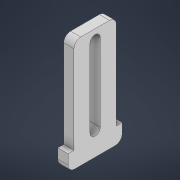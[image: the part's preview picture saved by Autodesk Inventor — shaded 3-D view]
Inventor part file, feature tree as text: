
AUTODESK INVENTOR PART (.ipt)
format: ipt  version: 2021 (Build 250183000, 183)  size: 122,368 bytes
history: native  units: mm
features: extrude x1, sketch x1
ambient origin geometry x8: Origin, YZ Plane, XZ Plane, XY Plane, X Axis, Y Axis, Z Axis, Center Point
bodies: Body1 (feature_tree)
feature tree (2):
  extrude  "Extrusion3"  Depth=2.0mm
  sketch  "Sketch1"  dims[d1=16.0mm d2=6.0mm d3=1.75mm d5=2.0mm d14=1.75mm d18=3.0mm d19=3.0mm d21=2.0mm d22=3.0mm d23=0.0mm d24=28.0mm d25=2.0mm]
